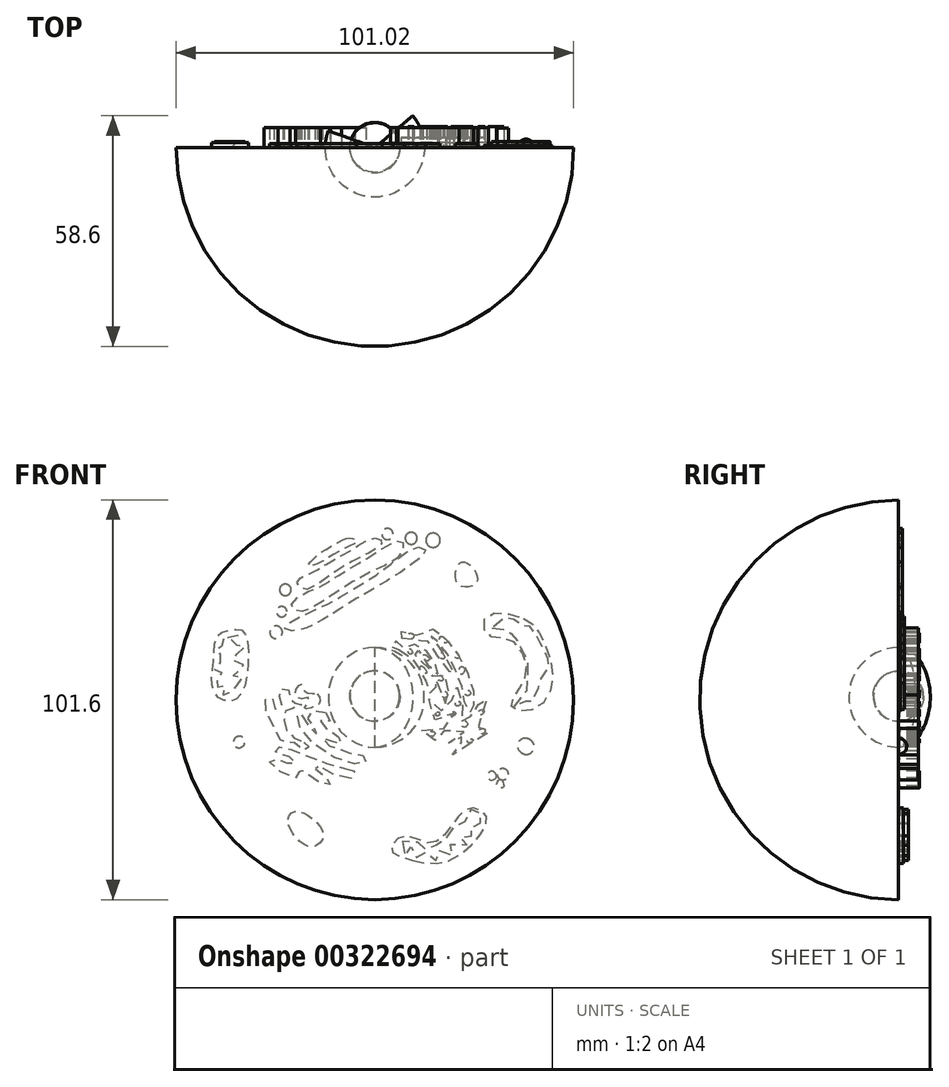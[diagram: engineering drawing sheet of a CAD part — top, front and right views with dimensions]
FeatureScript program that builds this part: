
annotation { "Feature Type Name" : "Feature", "Feature Type Description" : "" }
export const myFeature = defineFeature(function(context is Context, id is Id, definition is map)
    precondition{}
    {
        {
            var Q0;
            Q0=qCreatedBy(makeId("Front.planeOp"),FACE);
            var sketch = newSketch(context, id + "F0", { "sketchPlane" : qUnion([Q0])});
            skLineSegment(sketch, "E0", {"start": v(0, 0) * mm, "end": v(0, 12.7) * mm});
            skArc(sketch, "E1", {"start": v(0, 0) * mm, "mid": v(6.4, 6.35) * mm, "end": v(0, 12.7) * mm});
            skSolve(sketch);
        }
        {
            var Q0;
            Q0=makeQuery(id+"F0.imprint","IMPRINT",FACE,{"disambiguationData":[TD([[makeQuery(id+"F0.imprint","IMPRINT",EDGE,{"derivedFrom":sQuery(id+"F0.wireOp",EDGE,"E0")}),-1.0]])]});
            var Q1;
            Q1=sQuery(id+"F0.wireOp",EDGE,"E0");
            revolve(context, id + "F1", {"entities" : qUnion([Q0]), "axis" : qUnion([Q1]), "revolveType" : RevolveType.FULL});
        }
        {
            var Q0;
            Q0=qCreatedBy(makeId("Front.planeOp"),FACE);
            var sketch = newSketch(context, id + "F2", { "sketchPlane" : qUnion([Q0])});
            skLineSegment(sketch, "E2", {"start": v(0, -6.67) * mm, "end": v(0, 18.73) * mm});
            skArc(sketch, "E3", {"start": v(0, 18.73) * mm, "mid": v(-12.59, 6.03) * mm, "end": v(0, -6.67) * mm});
            skSolve(sketch);
        }
        {
            var Q0;
            Q0=makeQuery(id+"F2.imprint","IMPRINT",FACE,{"disambiguationData":[TD([[makeQuery(id+"F2.imprint","IMPRINT",EDGE,{"derivedFrom":sQuery(id+"F2.wireOp",EDGE,"E2")}),1.0]])]});
            var Q1;
            Q1=sQuery(id+"F2.wireOp",EDGE,"E2");
            revolve(context, id + "F3", {"entities" : qUnion([Q0]), "axis" : qUnion([Q1]), "revolveType" : RevolveType.TWO_DIRECTIONS, "angle" : 220 * degree, "angleBack" : 340 * degree});
        }
        {
            var Q0;
            Q0=qCreatedBy(makeId("Right.planeOp"),FACE);
            var sketch = newSketch(context, id + "F4", { "sketchPlane" : qUnion([Q0])});
            skLineSegment(sketch, "E4", {"start": v(0, 56.2) * mm, "end": v(0, -45.4) * mm});
            skArc(sketch, "E5", {"start": v(0, -45.4) * mm, "mid": v(50.5, 5.4) * mm, "end": v(0, 56.2) * mm});
            skSolve(sketch);
        }
        {
            var Q0;
            Q0=makeQuery(id+"F4.imprint","IMPRINT",FACE,{"disambiguationData":[TD([[makeQuery(id+"F4.imprint","IMPRINT",EDGE,{"derivedFrom":sQuery(id+"F4.wireOp",EDGE,"E4")}),1.0]])]});
            var Q1;
            Q1=sQuery(id+"F4.wireOp",EDGE,"E4");
            revolve(context, id + "F5", {"entities" : qUnion([Q0]), "axis" : qUnion([Q1]), "revolveType" : RevolveType.TWO_DIRECTIONS, "angle" : 270 * degree, "angleBack" : 90 * degree});
        }
        {
            var Q0;
            Q0=qCreatedBy(makeId("Front.planeOp"),FACE);
            var sketch = newSketch(context, id + "F6", { "sketchPlane" : qUnion([Q0])});
            skFitSpline(sketch, "E6", {"points": [v(9.6, -35.38) * mm, v(18.8, -35.51) * mm, v(27.69, -27.56) * mm, v(27.92, -23.4) * mm, v(23.7, -22.29) * mm, v(19.27, -26.96) * mm, v(14.13, -30.97) * mm, v(7.66, -29.22) * mm, v(4.07, -32.55) * mm, v(9.6, -35.38) * mm]});
            skSolve(sketch);
        }
        {
            var Q0;
            Q0 = qSketchRegion(id + "F6", true);
            extrude(context, id + "F7", {"entities" : qUnion([Q0]), "operationType" : NewBodyOperationType.ADD, "oppositeDirection" : true, "depth" : 1.27 * mm});
        }
        {
            var Q0;
            Q0=qCreatedBy(makeId("Front.planeOp"),FACE);
            var sketch = newSketch(context, id + "F8", { "sketchPlane" : qUnion([Q0])});
            skFitSpline(sketch, "E7", {"points": [v(-12.54, 2.24) * mm, v(-11.38, 0) * mm, v(-13.87, 0) * mm, v(-10.61, -3.1) * mm, v(-8.4, -4.96) * mm, v(-9.4, -6.04) * mm, v(-12.52, -4.21) * mm, v(-13.25, -4.93) * mm, v(-5.01, -8.38) * mm, v(-2.42, -9.05) * mm, v(-2.65, -10.58) * mm, v(-11.31, -8.74) * mm, v(-19.67, 0) * mm, v(-19.34, 2.33) * mm, v(-17.66, 0) * mm, v(-14.84, -3.26) * mm, v(-14.58, -2.7) * mm, v(-16.76, 0) * mm, v(-16.36, 2.24) * mm, v(-12.54, 2.24) * mm]});
            skSolve(sketch);
        }
        {
            var Q0;
            Q0 = qSketchRegion(id + "F8", true);
            extrude(context, id + "F9", {"entities" : qUnion([Q0]), "oppositeDirection" : true, "depth" : 5.08 * mm});
        }
        {
            var Q0;
            Q0=qCreatedBy(makeId("Front.planeOp"),FACE);
            var sketch = newSketch(context, id + "F10", { "sketchPlane" : qUnion([Q0])});
            skFitSpline(sketch, "E8", {"points": [v(-7.66, -12) * mm, v(-5.06, -12.89) * mm, v(-6.93, -14.76) * mm, v(-14.96, -11.24) * mm, v(-14.85, -12.41) * mm, v(-11.5, -15.13) * mm, v(-12, -16.47) * mm, v(-19.37, -12.16) * mm, v(-19.1, -13.6) * mm, v(-20.88, -14.36) * mm, v(-26.72, -10.14) * mm, v(-23.75, -9.96) * mm, v(-21.5, -10.92) * mm, v(-19.93, -10.03) * mm, v(-25.5, -7.67) * mm, v(-24.28, -6.65) * mm, v(-19.24, -8.06) * mm, v(-7.66, -12) * mm]});
            skSolve(sketch);
        }
        {
            var Q0;
            Q0 = qSketchRegion(id + "F10", true);
            extrude(context, id + "F11", {"entities" : qUnion([Q0]), "oppositeDirection" : true, "depth" : 5.08 * mm});
        }
        {
            var Q0;
            Q0=qCreatedBy(makeId("Front.planeOp"),FACE);
            var sketch = newSketch(context, id + "F12", { "sketchPlane" : qUnion([Q0])});
            skFitSpline(sketch, "E9", {"points": [v(-17.95, -5.44) * mm, v(-16.66, -6.4) * mm, v(-17.8, -7.6) * mm, v(-21.09, -5.17) * mm, v(-23, -5.57) * mm, v(-25.04, -2.63) * mm, v(-28.02, 4.97) * mm, v(-26.26, 5.94) * mm, v(-25.15, 2.95) * mm, v(-23.37, 4.5) * mm, v(-24.55, 7.26) * mm, v(-22.55, 8.42) * mm, v(-21.57, 6.57) * mm, v(-21.12, 4.79) * mm, v(-18.57, 4.3) * mm, v(-20.32, 3.37) * mm, v(-22.58, 2.7) * mm, v(-22.98, 0) * mm, v(-21.6, -3.48) * mm, v(-17.95, -5.44) * mm]});
            skSolve(sketch);
        }
        {
            var Q0;
            Q0 = qSketchRegion(id + "F12", true);
            extrude(context, id + "F13", {"entities" : qUnion([Q0]), "oppositeDirection" : true, "depth" : 5.08 * mm});
        }
        {
            var Q0;
            Q0=qCreatedBy(makeId("Front.planeOp"),FACE);
            var sketch = newSketch(context, id + "F14", { "sketchPlane" : qUnion([Q0])});
            skFitSpline(sketch, "E10", {"points": [v(-14.63, 6.86) * mm, v(-13.89, 4.93) * mm, v(-15.24, 3.7) * mm, v(-17.79, 3.21) * mm, v(-17, 4.7) * mm, v(-17.02, 5.09) * mm, v(-16.9, 5.99) * mm, v(-18.89, 5.63) * mm, v(-20.14, 7.6) * mm, v(-18.37, 9.4) * mm, v(-17.73, 7.4) * mm, v(-14.63, 6.86) * mm]});
            skSolve(sketch);
        }
        {
            var Q0;
            Q0 = qSketchRegion(id + "F14", true);
            extrude(context, id + "F15", {"entities" : qUnion([Q0]), "oppositeDirection" : true, "depth" : 5.08 * mm});
        }
        {
            var Q0;
            Q0=qCreatedBy(makeId("Front.planeOp"),FACE);
            var sketch = newSketch(context, id + "F16", { "sketchPlane" : qUnion([Q0])});
            skFitSpline(sketch, "E11", {"points": [v(6.06, 18.18) * mm, v(9.04, 16.45) * mm, v(10.42, 14.53) * mm, v(12.01, 12.23) * mm, v(13.1, 9.44) * mm, v(13.54, 7.45) * mm, v(15.68, 7.3) * mm, v(15.32, 9.12) * mm, v(14.84, 10.01) * mm, v(15.82, 10.44) * mm, v(16.73, 8.54) * mm, v(17.09, 5.02) * mm, v(18.51, 4.63) * mm, v(18.74, 7.34) * mm, v(17.99, 11.49) * mm, v(15.64, 11.5) * mm, v(14.6, 11.35) * mm, v(14.4, 12.08) * mm, v(12.35, 14.95) * mm, v(9.73, 17.64) * mm, v(10.7, 18.17) * mm, v(12.55, 15.85) * mm, v(14.8, 12.58) * mm, v(16.28, 12.09) * mm, v(16.18, 13.1) * mm, v(14.22, 15.94) * mm, v(12.17, 18.88) * mm, v(9.92, 19.42) * mm, v(8.6, 18.46) * mm, v(5.63, 19.43) * mm, v(5.5, 20.24) * mm, v(4.46, 20.6) * mm, v(4.1, 18.83) * mm, v(5.01, 18.62) * mm, v(6.06, 18.18) * mm]});
            skSolve(sketch);
        }
        {
            var Q0;
            Q0 = qSketchRegion(id + "F16", true);
            extrude(context, id + "F17", {"entities" : qUnion([Q0]), "operationType" : NewBodyOperationType.ADD, "oppositeDirection" : true, "depth" : 5.08 * mm});
        }
        {
            var Q0;
            Q0=makeQuery(id+"F5.opRevolve","CAP_FACE",FACE,{"disambiguationData":[OSD([sQuery(id+"F4.wireOp",EDGE,"E4"),sQuery(id+"F4.wireOp",EDGE,"E5")])],"isStart":false});
            var sketch = newSketch(context, id + "F18", { "sketchPlane" : qUnion([Q0])});
            skFitSpline(sketch, "E12", {"points": [v(-6.93, 21.04) * mm, v(-6.03, 22.56) * mm, v(-9.3, 22.38) * mm, v(-11.99, 21.66) * mm, v(-12.96, 22.73) * mm, v(-14.23, 23.62) * mm, v(-18.95, 19.87) * mm, v(-21.84, 15.47) * mm, v(-24.8, 8.95) * mm, v(-25.12, 4.58) * mm, v(-24.88, 2.71) * mm, v(-24.08, 2.18) * mm, v(-22.87, 4.23) * mm, v(-22.16, 8.57) * mm, v(-20.3, 13.3) * mm, v(-17.4, 18.62) * mm, v(-14.81, 21.23) * mm, v(-14.26, 21.66) * mm, v(-17.85, 16.4) * mm, v(-20.2, 11.52) * mm, v(-17.49, 14.4) * mm, v(-13.96, 19.62) * mm, v(-13.06, 20.69) * mm, v(-12.6, 20.53) * mm, v(-6.93, 21.04) * mm]});
            skSolve(sketch);
        }
        {
            var Q0;
            Q0 = qSketchRegion(id + "F18", true);
            extrude(context, id + "F19", {"entities" : qUnion([Q0]), "operationType" : NewBodyOperationType.ADD, "depth" : 5.08 * mm});
        }
        {
            var Q0;
            Q0=qCreatedBy(makeId("Front.planeOp"),FACE);
            var sketch = newSketch(context, id + "F20", { "sketchPlane" : qUnion([Q0])});
            skFitSpline(sketch, "E13", {"points": [v(20.84, 8.67) * mm, v(21.74, 6.16) * mm, v(22.38, 2.3) * mm, v(21.8, 0) * mm, v(22.9, 0) * mm, v(24.08, 0) * mm, v(24.52, 1.6) * mm, v(26.44, 2.81) * mm, v(26.19, 5.44) * mm, v(27.83, 6.55) * mm, v(28.46, 1.7) * mm, v(26.04, 0) * mm, v(25.74, -2.1) * mm, v(27.64, 0) * mm, v(28.43, -3.18) * mm, v(18.84, -8.59) * mm, v(21.9, -5.56) * mm, v(23.4, -4.19) * mm, v(22.73, -3.8) * mm, v(20.61, -5.18) * mm, v(19.24, -5.88) * mm, v(18.56, -4.71) * mm, v(22.72, -2.6) * mm, v(21.37, -1.88) * mm, v(15.94, -3.55) * mm, v(15.98, -4.69) * mm, v(13.97, -4.47) * mm, v(11.7, -2.4) * mm, v(15.05, -2.82) * mm, v(19.34, 0) * mm, v(20.2, 2) * mm, v(17.73, 0) * mm, v(13.69, 2.03) * mm, v(13.86, 5.65) * mm, v(15.47, 3.92) * mm, v(17.62, 2.44) * mm, v(19.7, 4.12) * mm, v(19.3, 8.32) * mm, v(20.84, 8.67) * mm]});
            skSolve(sketch);
        }
        {
            var Q0;
            Q0 = qSketchRegion(id + "F20", true);
            extrude(context, id + "F21", {"entities" : qUnion([Q0]), "operationType" : NewBodyOperationType.ADD, "oppositeDirection" : true, "depth" : 5.08 * mm});
        }
        {
            var Q0;
            Q0=qCreatedBy(makeId("Front.planeOp"),FACE);
            var sketch = newSketch(context, id + "F22", { "sketchPlane" : qUnion([Q0])});
            skFitSpline(sketch, "E14", {"points": [v(7.07, -30.62) * mm, v(6.9, -33.28) * mm, v(7.92, -34.2) * mm, v(8.44, -31.66) * mm, v(9.73, -32.89) * mm, v(9.74, -34.33) * mm, v(11.72, -34.5) * mm, v(12.04, -33.65) * mm, v(13.6, -33.47) * mm, v(14.29, -35) * mm, v(16.22, -35.2) * mm, v(15.97, -33.26) * mm, v(16.8, -32.85) * mm, v(18.72, -34.08) * mm, v(20.02, -33.63) * mm, v(18.97, -31.8) * mm, v(20.06, -31.08) * mm, v(22.97, -31.55) * mm, v(24.4, -30.22) * mm, v(21.38, -29.57) * mm, v(22.54, -29.08) * mm, v(25.5, -28.92) * mm, v(25.4, -27.59) * mm, v(24.24, -26.97) * mm, v(25.6, -25.93) * mm, v(27.53, -25.53) * mm, v(27.66, -23.5) * mm, v(25.06, -23.91) * mm, v(24.67, -22.5) * mm, v(22.51, -23.7) * mm, v(22.73, -25.94) * mm, v(20.31, -26.2) * mm, v(20.06, -28.48) * mm, v(19.4, -29.36) * mm, v(17.97, -29.29) * mm, v(18.21, -30.66) * mm, v(16.77, -30.55) * mm, v(16.38, -31.64) * mm, v(16.1, -31.85) * mm, v(14.58, -31.22) * mm, v(13.46, -32.32) * mm, v(12.07, -32.25) * mm, v(11.32, -30.59) * mm, v(9.9, -31.48) * mm, v(7.07, -30.62) * mm]});
            skSolve(sketch);
        }
        {
            var Q0;
            Q0 = qSketchRegion(id + "F22", true);
            extrude(context, id + "F23", {"entities" : qUnion([Q0]), "oppositeDirection" : true, "depth" : 2.54 * mm});
        }
        {
            var Q0;
            Q0=qCreatedBy(makeId("Front.planeOp"),FACE);
            var sketch = newSketch(context, id + "F24", { "sketchPlane" : qUnion([Q0])});
            skFitSpline(sketch, "E15", {"points": [v(-35.22, 23.3) * mm, v(-32.99, 22.24) * mm, v(-32.42, 11.9) * mm, v(-35.24, 5.52) * mm, v(-39.19, 5.61) * mm, v(-41.42, 9.47) * mm, v(-40.9, 15.68) * mm, v(-39.94, 21.72) * mm, v(-35.22, 23.3) * mm]});
            skSolve(sketch);
        }
        {
            var Q0;
            Q0 = qSketchRegion(id + "F24", true);
            extrude(context, id + "F25", {"entities" : qUnion([Q0]), "operationType" : NewBodyOperationType.ADD, "oppositeDirection" : true, "depth" : 1.27 * mm});
        }
        {
            var Q0;
            Q0=qCreatedBy(makeId("Front.planeOp"),FACE);
            var sketch = newSketch(context, id + "F26", { "sketchPlane" : qUnion([Q0])});
            skFitSpline(sketch, "E16", {"points": [v(-38.38, 20.87) * mm, v(-38.67, 18.96) * mm, v(-39.24, 18.98) * mm, v(-40.09, 18.38) * mm, v(-40.23, 17.4) * mm, v(-39.28, 16.97) * mm, v(-38.95, 15.21) * mm, v(-40.42, 14.18) * mm, v(-40.48, 12.66) * mm, v(-38.92, 12.44) * mm, v(-39.42, 11.1) * mm, v(-40.5, 10.1) * mm, v(-39.69, 8.63) * mm, v(-38.08, 9.1) * mm, v(-39.21, 7.42) * mm, v(-36.8, 6.47) * mm, v(-36.14, 8.7) * mm, v(-34.2, 9.35) * mm, v(-33.67, 11.04) * mm, v(-35.92, 11.36) * mm, v(-35.83, 12.33) * mm, v(-33.86, 12.88) * mm, v(-33.4, 14.34) * mm, v(-35.85, 15.27) * mm, v(-35.78, 16.74) * mm, v(-33.64, 17.72) * mm, v(-33.16, 19.57) * mm, v(-35.9, 19.2) * mm, v(-36.38, 20.65) * mm, v(-34.52, 21.67) * mm, v(-38.38, 20.87) * mm]});
            skSolve(sketch);
        }
        {
            var Q0;
            Q0 = qSketchRegion(id + "F26", true);
            extrude(context, id + "F27", {"entities" : qUnion([Q0]), "operationType" : NewBodyOperationType.ADD, "oppositeDirection" : true, "depth" : 1.5 * mm});
        }
        {
            var Q0;
            Q0=qCreatedBy(makeId("Front.planeOp"),FACE);
            var sketch = newSketch(context, id + "F28", { "sketchPlane" : qUnion([Q0])});
            skFitSpline(sketch, "E17", {"points": [v(37.75, 26.12) * mm, v(41.7, 22.44) * mm, v(45.2, 11.92) * mm, v(41.06, 3.27) * mm, v(34.92, 3.37) * mm, v(36.04, 7.2) * mm, v(38.63, 13.08) * mm, v(34.49, 20.58) * mm, v(28.75, 21.9) * mm, v(28.44, 26.66) * mm, v(37.75, 26.12) * mm]});
            skSolve(sketch);
        }
        {
            var Q0;
            Q0 = qSketchRegion(id + "F28", true);
            extrude(context, id + "F29", {"entities" : qUnion([Q0]), "oppositeDirection" : true, "depth" : 0.5 * mm});
        }
        {
            var Q0;
            Q0=qCreatedBy(makeId("Front.planeOp"),FACE);
            var sketch = newSketch(context, id + "F30", { "sketchPlane" : qUnion([Q0])});
            skFitSpline(sketch, "E18", {"points": [v(29.83, 23.6) * mm, v(30.19, 22.21) * mm, v(31.39, 22.03) * mm, v(32.26, 23.2) * mm, v(33.22, 23.04) * mm, v(32.58, 21.85) * mm, v(34.08, 21.4) * mm, v(34.63, 22.2) * mm, v(34.85, 22.63) * mm, v(35.43, 22.32) * mm, v(34.8, 21.05) * mm, v(36.21, 20.18) * mm, v(37.15, 21.3) * mm, v(37.6, 20.53) * mm, v(36.57, 19.54) * mm, v(37.25, 18.68) * mm, v(38.4, 19.02) * mm, v(38.9, 18.21) * mm, v(37.93, 17.62) * mm, v(38.37, 16.47) * mm, v(39.46, 16.76) * mm, v(39.75, 15.7) * mm, v(38.92, 15.13) * mm, v(39.08, 14.3) * mm, v(40.06, 13.87) * mm, v(39.85, 11.68) * mm, v(38.67, 11.52) * mm, v(39.05, 10.11) * mm, v(37.96, 8.9) * mm, v(38.6, 7.86) * mm, v(36.96, 6.94) * mm, v(35.52, 5.03) * mm, v(35.22, 3.78) * mm, v(36.92, 4.1) * mm, v(37.15, 5.33) * mm, v(38.18, 5.78) * mm, v(38.38, 4.54) * mm, v(38.07, 3.24) * mm, v(39.49, 3.18) * mm, v(40.06, 5.76) * mm, v(40.62, 7.11) * mm, v(42.37, 7.42) * mm, v(41.36, 8.74) * mm, v(41.48, 9.64) * mm, v(43.9, 9.75) * mm, v(41.84, 10.96) * mm, v(42.13, 11.7) * mm, v(44.15, 11.8) * mm, v(44.24, 13.71) * mm, v(42.74, 14.09) * mm, v(42.79, 14.46) * mm, v(44.01, 14.72) * mm, v(43.95, 15.78) * mm, v(42.66, 15.81) * mm, v(42.63, 16.3) * mm, v(43.36, 16.33) * mm, v(43.22, 17.8) * mm, v(42.25, 17.29) * mm, v(42.1, 17.97) * mm, v(42.8, 18.49) * mm, v(42.13, 19.74) * mm, v(41.25, 19.3) * mm, v(40.75, 19.89) * mm, v(41.66, 20.88) * mm, v(40.95, 21.92) * mm, v(39.68, 21.57) * mm, v(39.38, 21.84) * mm, v(39.86, 23.12) * mm, v(39.3, 24.07) * mm, v(38.02, 22.77) * mm, v(37.48, 22.87) * mm, v(37.74, 24.61) * mm, v(36.4, 23.03) * mm, v(35.73, 23.38) * mm, v(36.15, 25.1) * mm, v(34.5, 25.77) * mm, v(33.36, 24.07) * mm, v(32.87, 24.15) * mm, v(32.9, 26.22) * mm, v(31.21, 26.14) * mm, v(31.35, 24.36) * mm, v(29.83, 23.6) * mm]});
            skSolve(sketch);
        }
        {
            var Q0;
            Q0 = qSketchRegion(id + "F30", true);
            extrude(context, id + "F31", {"entities" : qUnion([Q0]), "oppositeDirection" : true, "depth" : 1.5 * mm});
        }
        {
            var Q0;
            Q0=qCreatedBy(makeId("Front.planeOp"),FACE);
            var sketch = newSketch(context, id + "F32", { "sketchPlane" : qUnion([Q0])});
            skFitSpline(sketch, "E19", {"points": [v(-8.18, 45.99) * mm, v(-6.17, 46.5) * mm, v(-4.6, 45.63) * mm, v(-7.3, 44.05) * mm, v(-13.05, 40.8) * mm, v(-16.9, 39.29) * mm, v(-15.03, 41.73) * mm, v(-8.18, 45.99) * mm]});
            skSolve(sketch);
        }
        {
            var Q0;
            Q0 = qSketchRegion(id + "F32", true);
            extrude(context, id + "F33", {"entities" : qUnion([Q0]), "operationType" : NewBodyOperationType.ADD, "oppositeDirection" : true, "depth" : 1 * mm});
        }
        {
            var Q0;
            Q0=qCreatedBy(makeId("Front.planeOp"),FACE);
            var sketch = newSketch(context, id + "F34", { "sketchPlane" : qUnion([Q0])});
            skFitSpline(sketch, "E20", {"points": [v(0, 46.47) * mm, v(1.88, 45.56) * mm, v(0, 43.6) * mm, v(-5.33, 40.8) * mm, v(-10.7, 37.52) * mm, v(-18.13, 33.43) * mm, v(-19.77, 35.4) * mm, v(-16.67, 37.39) * mm, v(-10.36, 41.02) * mm, v(-5.44, 43.76) * mm, v(0, 46.47) * mm]});
            skSolve(sketch);
        }
        {
            var Q0;
            Q0 = qSketchRegion(id + "F34", true);
            extrude(context, id + "F35", {"entities" : qUnion([Q0]), "oppositeDirection" : true, "depth" : 1 * mm});
        }
        {
            var Q0;
            Q0=qCreatedBy(makeId("Front.planeOp"),FACE);
            var sketch = newSketch(context, id + "F36", { "sketchPlane" : qUnion([Q0])});
            skFitSpline(sketch, "E21", {"points": [v(5.62, 45.69) * mm, v(7.2, 45.3) * mm, v(6.6, 42.24) * mm, v(-1.88, 37.45) * mm, v(-14.25, 29.75) * mm, v(-18.88, 27.86) * mm, v(-21.17, 28.8) * mm, v(-19.5, 31.54) * mm, v(-14.37, 33.94) * mm, v(-9.1, 37.08) * mm, v(-3.9, 40.2) * mm, v(0, 42.63) * mm, v(5.62, 45.69) * mm]});
            skSolve(sketch);
        }
        {
            var Q0;
            Q0 = qSketchRegion(id + "F36", true);
            extrude(context, id + "F37", {"entities" : qUnion([Q0]), "oppositeDirection" : true, "depth" : 1 * mm});
        }
        {
            var Q0;
            Q0=qCreatedBy(makeId("Front.planeOp"),FACE);
            var sketch = newSketch(context, id + "F38", { "sketchPlane" : qUnion([Q0])});
            skFitSpline(sketch, "E22", {"points": [v(11.13, 44.25) * mm, v(12.91, 43.24) * mm, v(10.64, 40.7) * mm, v(3.6, 35.95) * mm, v(-7.41, 29.39) * mm, v(-19.44, 23) * mm, v(-22.92, 23.5) * mm, v(-19.3, 26.3) * mm, v(-12.19, 29.64) * mm, v(-5.7, 33.39) * mm, v(1.65, 38.03) * mm, v(11.13, 44.25) * mm]});
            skSolve(sketch);
        }
        {
            var Q0;
            Q0 = qSketchRegion(id + "F38", true);
            extrude(context, id + "F39", {"entities" : qUnion([Q0]), "oppositeDirection" : true, "depth" : 1 * mm});
        }
        {
            var Q0;
            Q0=qCreatedBy(makeId("Front.planeOp"),FACE);
            var sketch = newSketch(context, id + "F40", { "sketchPlane" : qUnion([Q0])});
            skCircle(sketch, "E23", {"center": v(-22.73, 33.32) * mm, "radius": 1.46 * mm});
            skSolve(sketch);
        }
        {
            var Q0;
            Q0 = qSketchRegion(id + "F40", true);
            extrude(context, id + "F41", {"entities" : qUnion([Q0]), "operationType" : NewBodyOperationType.ADD, "oppositeDirection" : true, "depth" : 1 * mm});
        }
        {
            var Q0;
            Q0=qCreatedBy(makeId("Front.planeOp"),FACE);
            var sketch = newSketch(context, id + "F42", { "sketchPlane" : qUnion([Q0])});
            skCircle(sketch, "E24", {"center": v(-23.65, 27.79) * mm, "radius": 1.32 * mm});
            skSolve(sketch);
        }
        {
            var Q0;
            Q0 = qSketchRegion(id + "F42", true);
            extrude(context, id + "F43", {"entities" : qUnion([Q0]), "oppositeDirection" : true, "depth" : 1 * mm});
        }
        {
            var Q0;
            Q0=qCreatedBy(makeId("Front.planeOp"),FACE);
            var sketch = newSketch(context, id + "F44", { "sketchPlane" : qUnion([Q0])});
            skCircle(sketch, "E25", {"center": v(3.24, 47.5) * mm, "radius": 1.44 * mm});
            skSolve(sketch);
        }
        {
            var Q0;
            Q0 = qSketchRegion(id + "F44", true);
            extrude(context, id + "F45", {"entities" : qUnion([Q0]), "oppositeDirection" : true, "depth" : 1 * mm});
        }
        {
            var Q0;
            Q0=qCreatedBy(makeId("Front.planeOp"),FACE);
            var sketch = newSketch(context, id + "F46", { "sketchPlane" : qUnion([Q0])});
            skCircle(sketch, "E26", {"center": v(9.24, 46.43) * mm, "radius": 1.53 * mm});
            skSolve(sketch);
        }
        {
            var Q0;
            Q0 = qSketchRegion(id + "F46", true);
            extrude(context, id + "F47", {"entities" : qUnion([Q0]), "operationType" : NewBodyOperationType.ADD, "oppositeDirection" : true, "depth" : 1 * mm});
        }
        {
            var Q0;
            Q0=qCreatedBy(makeId("Front.planeOp"),FACE);
            var sketch = newSketch(context, id + "F48", { "sketchPlane" : qUnion([Q0])});
            skCircle(sketch, "E27", {"center": v(-25.08, 22.56) * mm, "radius": 1.6 * mm});
            skSolve(sketch);
        }
        {
            var Q0;
            Q0 = qSketchRegion(id + "F48", true);
            extrude(context, id + "F49", {"entities" : qUnion([Q0]), "oppositeDirection" : true, "depth" : 1 * mm});
        }
        {
            var Q0;
            Q0=qCreatedBy(makeId("Front.planeOp"),FACE);
            var sketch = newSketch(context, id + "F50", { "sketchPlane" : qUnion([Q0])});
            skCircle(sketch, "E28", {"center": v(14.8, 45.94) * mm, "radius": 1.81 * mm});
            skSolve(sketch);
        }
        {
            var Q0;
            Q0 = qSketchRegion(id + "F50", true);
            extrude(context, id + "F51", {"entities" : qUnion([Q0]), "operationType" : NewBodyOperationType.ADD, "oppositeDirection" : true, "depth" : 1 * mm});
        }
        {
            var Q0;
            Q0=qCreatedBy(makeId("Front.planeOp"),FACE);
            var sketch = newSketch(context, id + "F52", { "sketchPlane" : qUnion([Q0])});
            skFitSpline(sketch, "E29", {"points": [v(21.61, 40.1) * mm, v(23.48, 40.1) * mm, v(25.85, 37.42) * mm, v(25.49, 34.76) * mm, v(22.1, 34.25) * mm, v(20.5, 36.24) * mm, v(21.61, 40.1) * mm]});
            skSolve(sketch);
        }
        {
            var Q0;
            Q0 = qSketchRegion(id + "F52", true);
            extrude(context, id + "F53", {"entities" : qUnion([Q0]), "oppositeDirection" : true, "depth" : 1 * mm});
        }
        {
            var Q0;
            Q0=qCreatedBy(makeId("Front.planeOp"),FACE);
            var sketch = newSketch(context, id + "F54", { "sketchPlane" : qUnion([Q0])});
            skFitSpline(sketch, "E30", {"points": [v(-22.02, -25.03) * mm, v(-20.3, -23) * mm, v(-15.65, -24.92) * mm, v(-13.11, -29.2) * mm, v(-15.6, -31.93) * mm, v(-19.86, -29.8) * mm, v(-22.02, -25.03) * mm]});
            skSolve(sketch);
        }
        {
            var Q0;
            Q0 = qSketchRegion(id + "F54", true);
            extrude(context, id + "F55", {"entities" : qUnion([Q0]), "oppositeDirection" : true, "depth" : 1 * mm});
        }
        {
            var Q0;
            Q0=makeQuery(id+"F5.opRevolve","CAP_FACE",FACE,{"disambiguationData":[OSD([sQuery(id+"F4.wireOp",EDGE,"E4"),sQuery(id+"F4.wireOp",EDGE,"E5")])],"isStart":false});
            var sketch = newSketch(context, id + "F56", { "sketchPlane" : qUnion([Q0])});
            skSolve(sketch);
        }
        {
            var Q0;
            Q0=qCreatedBy(makeId("Front.planeOp"),FACE);
            var sketch = newSketch(context, id + "F57", { "sketchPlane" : qUnion([Q0])});
            skLineSegment(sketch, "E31", {"start": v(39.43, -4.78) * mm, "end": v(37.32, -8.07) * mm});
            skArc(sketch, "E32", {"start": v(39.43, -4.78) * mm, "mid": v(36.58, -5.27) * mm, "end": v(37.32, -8.07) * mm});
            skSolve(sketch);
        }
        {
            var Q0;
            Q0 = qSketchRegion(id + "F57", true);
            var Q1;
            Q1=sQuery(id+"F57.wireOp",EDGE,"E31");
            revolve(context, id + "F58", {"operationType" : NewBodyOperationType.ADD, "entities" : qUnion([Q0]), "axis" : qUnion([Q1]), "revolveType" : RevolveType.FULL});
        }
        {
            var Q0;
            Q0=qCreatedBy(makeId("Front.planeOp"),FACE);
            var sketch = newSketch(context, id + "F59", { "sketchPlane" : qUnion([Q0])});
            skLineSegment(sketch, "E33", {"start": v(-33.64, -4.1) * mm, "end": v(-35.31, -6.59) * mm});
            skArc(sketch, "E34", {"start": v(-33.64, -4.1) * mm, "mid": v(-35.68, -4.53) * mm, "end": v(-35.31, -6.59) * mm});
            skSolve(sketch);
        }
        {
            var Q0;
            Q0 = qSketchRegion(id + "F59", true);
            var Q1;
            Q1=sQuery(id+"F59.wireOp",EDGE,"E33");
            revolve(context, id + "F60", {"operationType" : NewBodyOperationType.ADD, "entities" : qUnion([Q0]), "axis" : qUnion([Q1]), "revolveType" : RevolveType.FULL});
        }
        {
            var Q0;
            Q0=qCreatedBy(makeId("Front.planeOp"),FACE);
            var sketch = newSketch(context, id + "F61", { "sketchPlane" : qUnion([Q0])});
            skCircle(sketch, "E35", {"center": v(32.52, -13.52) * mm, "radius": 1.44 * mm});
            skSolve(sketch);
        }
        {
            var Q0;
            Q0 = qSketchRegion(id + "F61", true);
            extrude(context, id + "F62", {"entities" : qUnion([Q0]), "oppositeDirection" : true, "depth" : 5 * mm});
        }
        {
            var Q0;
            Q0=makeQuery(id+"F21.opExtrude","CAP_FACE",FACE,{"disambiguationData":[OSD([sQuery(id+"F20.wireOp",EDGE,"E13")])],"isStart":false});
            var sketch = newSketch(context, id + "F63", { "sketchPlane" : qUnion([Q0])});
            skFitSpline(sketch, "E36", {"points": [v(-15.85, 2.32) * mm, v(-16.49, 2) * mm, v(-16.2, 1.36) * mm, v(-15.5, 1.52) * mm, v(-15.85, 2.32) * mm]});
            skSolve(sketch);
        }
        {
            var Q0;
            Q0 = qSketchRegion(id + "F63", true);
            extrude(context, id + "F64", {"entities" : qUnion([Q0]), "depth" : 0.2 * mm});
        }
        {
            var Q0;
            Q0=qCreatedBy(makeId("Front.planeOp"),FACE);
            var sketch = newSketch(context, id + "F65", { "sketchPlane" : qUnion([Q0])});
            skFitSpline(sketch, "E37", {"points": [v(21.33, 5) * mm, v(21.76, 4.5) * mm, v(21.22, 3.8) * mm, v(20.44, 4.33) * mm, v(21.33, 5) * mm]});
            skSolve(sketch);
        }
        {
            var Q0;
            Q0 = qSketchRegion(id + "F65", true);
            extrude(context, id + "F66", {"entities" : qUnion([Q0]), "oppositeDirection" : true, "depth" : 5.3 * mm});
        }
        {
            var Q0;
            Q0=qCreatedBy(makeId("Front.planeOp"),FACE);
            var sketch = newSketch(context, id + "F67", { "sketchPlane" : qUnion([Q0])});
            skFitSpline(sketch, "E38", {"points": [v(19.7, 2.28) * mm, v(20.32, 2.25) * mm, v(20.4, 1.62) * mm, v(19.5, 1.28) * mm, v(19.7, 2.28) * mm]});
            skSolve(sketch);
        }
        {
            var Q0;
            Q0 = qSketchRegion(id + "F67", true);
            extrude(context, id + "F68", {"entities" : qUnion([Q0]), "oppositeDirection" : true, "depth" : 5.3 * mm});
        }
        {
            var Q0;
            Q0=qCreatedBy(makeId("Front.planeOp"),FACE);
            var sketch = newSketch(context, id + "F69", { "sketchPlane" : qUnion([Q0])});
            skFitSpline(sketch, "E39", {"points": [v(22.88, 0) * mm, v(23.49, -1.07) * mm, v(22.32, -1.42) * mm, v(22.88, 0) * mm]});
            skSolve(sketch);
        }
        {
            var Q0;
            Q0 = qSketchRegion(id + "F69", true);
            extrude(context, id + "F70", {"entities" : qUnion([Q0]), "oppositeDirection" : true, "depth" : 5.3 * mm});
        }
        {
            var Q0;
            Q0=qCreatedBy(makeId("Front.planeOp"),FACE);
            var sketch = newSketch(context, id + "F71", { "sketchPlane" : qUnion([Q0])});
            skFitSpline(sketch, "E40", {"points": [v(24.33, -4.5) * mm, v(24.96, -4.85) * mm, v(24.1, -5.56) * mm, v(23.48, -5.14) * mm, v(24.33, -4.5) * mm]});
            skSolve(sketch);
        }
        {
            var Q0;
            Q0 = qSketchRegion(id + "F71", true);
            extrude(context, id + "F72", {"entities" : qUnion([Q0]), "oppositeDirection" : true, "depth" : 5.3 * mm});
        }
        {
            var Q0;
            Q0=qCreatedBy(makeId("Front.planeOp"),FACE);
            var sketch = newSketch(context, id + "F73", { "sketchPlane" : qUnion([Q0])});
            skFitSpline(sketch, "E41", {"points": [v(26.45, 2.5) * mm, v(27.51, 2.82) * mm, v(27.56, 1.99) * mm, v(26.39, 1.51) * mm, v(26.45, 2.5) * mm]});
            skSolve(sketch);
        }
        {
            var Q0;
            Q0 = qSketchRegion(id + "F73", true);
            extrude(context, id + "F74", {"entities" : qUnion([Q0]), "oppositeDirection" : true, "depth" : 5.3 * mm});
        }
        {
            var Q0;
            Q0=qCreatedBy(makeId("Front.planeOp"),FACE);
            var sketch = newSketch(context, id + "F75", { "sketchPlane" : qUnion([Q0])});
            skFitSpline(sketch, "E42", {"points": [v(22.03, 13.9) * mm, v(22.77, 12.6) * mm, v(21.48, 11.93) * mm, v(22.03, 13.9) * mm]});
            skSolve(sketch);
        }
        {
            var Q0;
            Q0 = qSketchRegion(id + "F75", true);
            extrude(context, id + "F76", {"entities" : qUnion([Q0]), "oppositeDirection" : true, "depth" : 5.3 * mm});
        }
        {
            var Q0;
            Q0=qCreatedBy(makeId("Front.planeOp"),FACE);
            var sketch = newSketch(context, id + "F77", { "sketchPlane" : qUnion([Q0])});
            skFitSpline(sketch, "E43", {"points": [v(16.93, 21.53) * mm, v(18.3, 20.02) * mm, v(16.64, 20.3) * mm, v(16.93, 21.53) * mm]});
            skSolve(sketch);
        }
        {
            var Q0;
            Q0 = qSketchRegion(id + "F77", true);
            extrude(context, id + "F78", {"entities" : qUnion([Q0]), "oppositeDirection" : true, "depth" : 5.3 * mm});
        }
        {
            var Q0;
            Q0=qCreatedBy(makeId("Front.planeOp"),FACE);
            var sketch = newSketch(context, id + "F79", { "sketchPlane" : qUnion([Q0])});
            skFitSpline(sketch, "E44", {"points": [v(8.6, 22.14) * mm, v(9.88, 21.88) * mm, v(9.19, 20.81) * mm, v(8.6, 22.14) * mm]});
            skSolve(sketch);
        }
        {
            var Q0;
            Q0 = qSketchRegion(id + "F79", true);
            extrude(context, id + "F80", {"entities" : qUnion([Q0]), "oppositeDirection" : true, "depth" : 5.3 * mm});
        }
        {
            var Q0;
            Q0=qCreatedBy(makeId("Front.planeOp"),FACE);
            var sketch = newSketch(context, id + "F81", { "sketchPlane" : qUnion([Q0])});
            skFitSpline(sketch, "E45", {"points": [v(11.6, 13.88) * mm, v(12.47, 13.65) * mm, v(13.07, 12.14) * mm, v(11.74, 12.9) * mm, v(11.6, 13.88) * mm]});
            skSolve(sketch);
        }
        {
            var Q0;
            Q0 = qSketchRegion(id + "F81", true);
            extrude(context, id + "F82", {"entities" : qUnion([Q0]), "oppositeDirection" : true, "depth" : 5.3 * mm});
        }
        {
            var Q0;
            Q0=qCreatedBy(makeId("Front.planeOp"),FACE);
            var sketch = newSketch(context, id + "F83", { "sketchPlane" : qUnion([Q0])});
            skFitSpline(sketch, "E46", {"points": [v(16.47, 11.5) * mm, v(17.09, 11.3) * mm, v(17.14, 10.29) * mm, v(15.92, 10.62) * mm, v(16.47, 11.5) * mm]});
            skSolve(sketch);
        }
        {
            var Q0;
            Q0 = qSketchRegion(id + "F83", true);
            extrude(context, id + "F84", {"entities" : qUnion([Q0]), "oppositeDirection" : true, "depth" : 5.3 * mm});
        }
        {
            var Q0;
            Q0=qCreatedBy(makeId("Front.planeOp"),FACE);
            var sketch = newSketch(context, id + "F85", { "sketchPlane" : qUnion([Q0])});
            skFitSpline(sketch, "E47", {"points": [v(8.77, 18.39) * mm, v(9.5, 17.23) * mm, v(8.65, 17.17) * mm, v(8.77, 18.39) * mm]});
            skSolve(sketch);
        }
        {
            var Q0;
            Q0 = qSketchRegion(id + "F85", true);
            extrude(context, id + "F86", {"entities" : qUnion([Q0]), "oppositeDirection" : true, "depth" : 5.3 * mm});
        }
        {
            var Q0;
            Q0=qCreatedBy(makeId("Front.planeOp"),FACE);
            var sketch = newSketch(context, id + "F87", { "sketchPlane" : qUnion([Q0])});
            skFitSpline(sketch, "E48", {"points": [v(23.63, 7.86) * mm, v(24.25, 6.8) * mm, v(23.11, 6.62) * mm, v(23.63, 7.86) * mm]});
            skSolve(sketch);
        }
        {
            var Q0;
            Q0 = qSketchRegion(id + "F87", true);
            extrude(context, id + "F88", {"entities" : qUnion([Q0]), "oppositeDirection" : true, "depth" : 5.3 * mm});
        }
        {
            var Q0;
            Q0=qCreatedBy(makeId("Front.planeOp"),FACE);
            var sketch = newSketch(context, id + "F89", { "sketchPlane" : qUnion([Q0])});
            skFitSpline(sketch, "E49", {"points": [v(16.76, 17.48) * mm, v(17.74, 16.16) * mm, v(16.92, 15.89) * mm, v(16.76, 17.48) * mm]});
            skSolve(sketch);
        }
        {
            var Q0;
            Q0 = qSketchRegion(id + "F89", true);
            extrude(context, id + "F90", {"entities" : qUnion([Q0]), "oppositeDirection" : true, "depth" : 5.3 * mm});
        }
        {
            var Q0;
            Q0=qCreatedBy(makeId("Front.planeOp"),FACE);
            var sketch = newSketch(context, id + "F91", { "sketchPlane" : qUnion([Q0])});
            skFitSpline(sketch, "E50", {"points": [v(12.42, 16.85) * mm, v(13.87, 15.72) * mm, v(12.87, 15.42) * mm, v(12.42, 16.85) * mm]});
            skSolve(sketch);
        }
        {
            var Q0;
            Q0 = qSketchRegion(id + "F91", true);
            extrude(context, id + "F92", {"entities" : qUnion([Q0]), "oppositeDirection" : true, "depth" : 5.3 * mm});
        }
        {
            var Q0;
            {var subQ0=sQuery(id+"F4.wireOp",EDGE,"E5");Q0=makeQuery(id+"F56.imprint","IMPRINT",FACE,{"disambiguationData":[TD([[makeQuery(id+"F56.imprint","IMPRINT",EDGE,{"derivedFrom":makeQuery(id+"F5.opRevolve","CAP_EDGE",EDGE,{"disambiguationData":[OSD([subQ0])],"isStart":true})}),-1.0]])]});}
            var sketch = newSketch(context, id + "F93", { "sketchPlane" : qUnion([Q0])});
            skFitSpline(sketch, "E51", {"points": [v(-26.67, -2.2) * mm, v(-27.92, -2.14) * mm, v(-27.41, -3.23) * mm, v(-26.67, -2.2) * mm]});
            skSolve(sketch);
        }
        {
            var Q0;
            Q0 = qSketchRegion(id + "F93", true);
            extrude(context, id + "F94", {"entities" : qUnion([Q0]), "depth" : 5.3 * mm});
        }
        {
            var Q0;
            Q0=qCreatedBy(makeId("Front.planeOp"),FACE);
            var sketch = newSketch(context, id + "F95", { "sketchPlane" : qUnion([Q0])});
            skFitSpline(sketch, "E52", {"points": [v(17.78, 7.58) * mm, v(18.4, 6.33) * mm, v(17.4, 6.08) * mm, v(17.78, 7.58) * mm]});
            skSolve(sketch);
        }
        {
            var Q0;
            Q0 = qSketchRegion(id + "F95", true);
            extrude(context, id + "F96", {"entities" : qUnion([Q0]), "oppositeDirection" : true, "depth" : 5.3 * mm});
        }
        {
            var Q0;
            Q0=qCreatedBy(makeId("Front.planeOp"),FACE);
            var sketch = newSketch(context, id + "F97", { "sketchPlane" : qUnion([Q0])});
            skFitSpline(sketch, "E53", {"points": [v(14.12, -2.77) * mm, v(15.27, -3.05) * mm, v(14.3, -3.92) * mm, v(14.12, -2.77) * mm]});
            skSolve(sketch);
        }
        {
            var Q0;
            Q0 = qSketchRegion(id + "F97", true);
            extrude(context, id + "F98", {"entities" : qUnion([Q0]), "oppositeDirection" : true, "depth" : 5.3 * mm});
        }
        {
            var Q0;
            Q0=qCreatedBy(makeId("Front.planeOp"),FACE);
            var sketch = newSketch(context, id + "F99", { "sketchPlane" : qUnion([Q0])});
            skFitSpline(sketch, "E54", {"points": [v(20.45, 17.62) * mm, v(21.38, 16.23) * mm, v(20.56, 16.08) * mm, v(20.45, 17.62) * mm]});
            skSolve(sketch);
        }
        {
            var Q0;
            Q0 = qSketchRegion(id + "F99", true);
            extrude(context, id + "F100", {"entities" : qUnion([Q0]), "oppositeDirection" : true, "depth" : 5.3 * mm});
        }
        {
            var Q0;
            Q0=qCreatedBy(makeId("Front.planeOp"),FACE);
            var sketch = newSketch(context, id + "F101", { "sketchPlane" : qUnion([Q0])});
            skFitSpline(sketch, "E55", {"points": [v(31.94, -14.8) * mm, v(32.76, -16.7) * mm, v(32.18, -17.01) * mm, v(31.69, -16.91) * mm, v(31.38, -16.6) * mm, v(30.93, -16.2) * mm, v(31.94, -14.8) * mm]});
            skSolve(sketch);
        }
        {
            var Q0;
            Q0 = qSketchRegion(id + "F101", true);
            extrude(context, id + "F102", {"entities" : qUnion([Q0]), "oppositeDirection" : true, "depth" : 5.3 * mm});
        }
        {
            var Q0;
            Q0=qCreatedBy(makeId("Front.planeOp"),FACE);
            var sketch = newSketch(context, id + "F103", { "sketchPlane" : qUnion([Q0])});
            skFitSpline(sketch, "E56", {"points": [v(30.87, -14.16) * mm, v(29.82, -12.74) * mm, v(28.87, -13.35) * mm, v(29.29, -15) * mm, v(30.87, -14.16) * mm]});
            skSolve(sketch);
        }
        {
            var Q0;
            Q0 = qSketchRegion(id + "F103", true);
            extrude(context, id + "F104", {"entities" : qUnion([Q0]), "operationType" : NewBodyOperationType.ADD, "oppositeDirection" : true, "depth" : 5.3 * mm});
        }
    });
